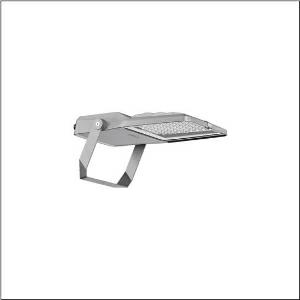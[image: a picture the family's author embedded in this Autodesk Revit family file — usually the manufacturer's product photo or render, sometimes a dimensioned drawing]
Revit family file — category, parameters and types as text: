
# Revit family: floodlight_fl_21_mini___pl64_5xa7776d2e1a_08ea
name_source: partatom
category: Lighting Fixtures
units: mm (PartAtom-declared; Revit-internal decimal feet)

## family parameters
Cut with Voids When Loaded = No
Host = Face
Light Source = No
Part Type = Normal
Room Calculation Point = No
Round Connector Dimension = Use Diameter
Shared = No

## types (1)
- --- (1 x LED, 17220 lm, 142.9 W, 3000K)
    Apparent Load = 143 VA
    CIE Flux Codes = 28 80 98 100 100
    Color Rendering = 70
    Color Temperature = 3000K
    Default Elevation = 1800 mm
    Description = Floodlight FL 21 mini, floodlight, primary light control with lens, of PMMA, primary optical cover: protective disc, of toughened safety glass, transparent, light distribution: PL64, light emission: direct distribution, installation type: surface-mounted, LED, High Power LED, rated luminous flux: 17.220lm, luminous efficacy: 121lm/W, light colour: 730, colour temperature: 3000K, control gear: Smart Interface (Zhaga), control: flexible luminous flux parameterisation, time-dependent luminous flux control, constant luminous flux control, overheat protection, pre-setting: logarithmic dimming characteristic, with terminal, 6-pole, mains connection: 220..240V, AC, 50/60Hz, start of lifetime: 143W, end of service life: 151W, reduction: 63W, luminaire housing, of diecast aluminium, powder-coated, Siteco® metallic grey (DB 702S), corrosivity category C5 mid according to DIN EN ISO 12944, suitable for swimming pools, chlorine-resistant, sealing non-destructively replaceable, mounting bracket, of steel, galvanised, powder-coated, Siteco® metallic grey (DB 702S), Smart Interface below and above, protection rating (complete): IP66, insulation class (complete): insulation class II (safety insulation), certification: CE, ENEC, VDE, protection symbol: D, impact resistance: IK08, permissible operating ambient temperature: -40..+40°C, permissible operating ambient temperature for outdoor applications: -40..+50°C, standard: DIN EN 12944, LABS conformity tested according to VDMA 24364:2018-05, packaging unit: 1 piece

Light Distribution: PL64
    Height = 70 mm
    Lamp = 1 x LED
    Lamp Light Flux = 17220 lm
    Lamp Power = 142.9 W
    Lamp count = 1
    Length = 485 mm
    Luminous efficacy = 121 lm/W
    Manufacturer = Siteco
    ModVariant = No
    Model = 5XA7776D2E1A
    Number of Poles = 1
    OnlyDefault = Yes
    Power Factor = 1
    Product Name = Floodlight FL 21 mini | PL64
    Product group = floodlight | pylon annexe
    ProductGroupID = 6200
    Protection Class = Protection class II
    Protection Degree = IP 66
    RLX_Detail_Level = 1
    RLX_Emergency_Light_Flux = 0 lm
    RLX_Emergency_Type = 0
    RLX_Emergency_Type_DB = No
    RlxData = <blob elided: 96441 chars, md5=afe55dbc>
    Socket = socket
    Standby Power = 0 W
    System Light Flux = 17220 lm
    System Power = 143 W
    Type Comments = factory setting: luminous flux: 100 % | dim-lin: 254 | 730 mA
    Type Image = l_1006845.jpg
    URL = http://relux.com
    VarID = @adj_165240
    Voltage = 0 V
    Weight = 0.00 kg
    Width = 337 mm

## geometry (parser evidence)
native form markers: Blend x4, Sweep x12
no freeform markers — native parametric forms only
